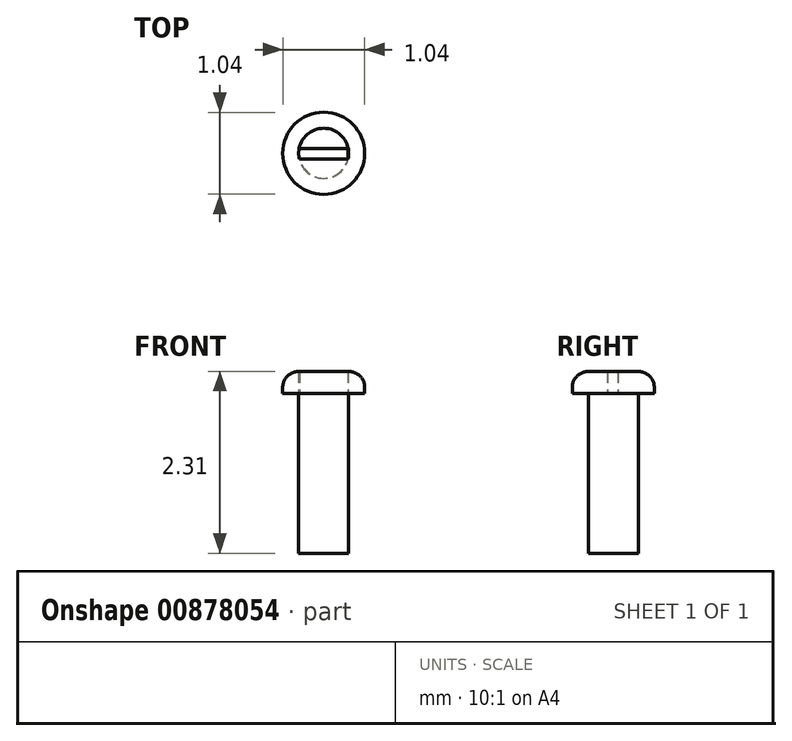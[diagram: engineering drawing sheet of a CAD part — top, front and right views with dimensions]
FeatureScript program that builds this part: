
annotation { "Feature Type Name" : "Feature", "Feature Type Description" : "" }
export const myFeature = defineFeature(function(context is Context, id is Id, definition is map)
    precondition{}
    {
        {
            var Q0;
            Q0=qCreatedBy(makeId("Top.planeOp"),FACE);
            var sketch = newSketch(context, id + "F0", { "sketchPlane" : qUnion([Q0])});
            skCircle(sketch, "E0", {"center": v(0, 0) * mm, "radius": 0.32 * mm});
            skCircle(sketch, "E1", {"center": v(0, 0) * mm, "radius": 0.52 * mm});
            skLineSegment(sketch, "E2.bottom", {"start": v(-0.31, 0.06) * mm, "end": v(0.31, 0.06) * mm});
            skLineSegment(sketch, "E2.top", {"start": v(-0.31, -0.07) * mm, "end": v(0.31, -0.07) * mm});
            skLineSegment(sketch, "E2.left", {"start": v(-0.31, 0.06) * mm, "end": v(-0.31, -0.07) * mm});
            skLineSegment(sketch, "E2.right", {"start": v(0.31, 0.06) * mm, "end": v(0.31, -0.07) * mm});
            skSolve(sketch);
        }
        {
            var Q0;
            {var subQ0=sQuery(id+"F0.wireOp",EDGE,"E2.bottom");Q0=makeQuery(id+"F0.imprint","IMPRINT",FACE,{"disambiguationData":[TD([[makeQuery(id+"F0.imprint","IMPRINT",EDGE,{"derivedFrom":subQ0}),1.0]])]});}
            var Q1;
            {var subQ0=sQuery(id+"F0.wireOp",EDGE,"E2.top");var subQ1=sQuery(id+"F0.wireOp",EDGE,"E0");var subQ3=makeQuery(id+"F0.imprint","INTERSECT",VERTEX,{"derivedFrom":[subQ1,subQ0]});Q1=makeQuery(id+"F0.imprint","IMPRINT",FACE,{"disambiguationData":[TD([[makeQuery(id+"F0.imprint","IMPRINT",EDGE,{"disambiguationData":[TD([[subQ3,-1.0]])],"derivedFrom":subQ1}),1.0]])]});}
            var Q2;
            {var subQ1=sQuery(id+"F0.wireOp",EDGE,"E2.bottom");Q2=makeQuery(id+"F0.imprint","IMPRINT",FACE,{"disambiguationData":[TD([[makeQuery(id+"F0.imprint","IMPRINT",EDGE,{"derivedFrom":subQ1}),-1.0]])]});}
            var Q3;
            {var subQ0=sQuery(id+"F0.wireOp",EDGE,"E2.left");var subQ1=sQuery(id+"F0.wireOp",EDGE,"E0");var subQ3=makeQuery(id+"F0.imprint","INTERSECT",VERTEX,{"derivedFrom":[subQ1,subQ0]});Q3=makeQuery(id+"F0.imprint","IMPRINT",FACE,{"disambiguationData":[TD([[makeQuery(id+"F0.imprint","IMPRINT",EDGE,{"disambiguationData":[TD([[subQ3,1.0]])],"derivedFrom":subQ1}),1.0]])]});}
            extrude(context, id + "F1", {"entities" : qUnion([Q0, Q1, Q2, Q3]), "oppositeDirection" : true, "depth" : 2.03 * mm, "offsetDistance" : 25.4 * mm});
        }
        {
            var Q0;
            Q0 = qSketchRegion(id + "F0", true);
            var Q1;
            {var subQ0=sQuery(id+"F0.wireOp",EDGE,"E2.left");var subQ1=sQuery(id+"F0.wireOp",EDGE,"E0");var subQ2=makeQuery(id+"F0.imprint","INTERSECT",VERTEX,{"derivedFrom":[subQ1,subQ0]});Q1=makeQuery(id+"F0.imprint","IMPRINT",FACE,{"disambiguationData":[TD([[makeQuery(id+"F0.imprint","IMPRINT",EDGE,{"disambiguationData":[TD([[subQ2,-1.0]])],"derivedFrom":subQ1}),-1.0]])]});}
            var Q2;
            {var subQ0=sQuery(id+"F0.wireOp",EDGE,"E2.top");var subQ1=sQuery(id+"F0.wireOp",EDGE,"E0");var subQ3=makeQuery(id+"F0.imprint","INTERSECT",VERTEX,{"derivedFrom":[subQ1,subQ0]});Q2=makeQuery(id+"F0.imprint","IMPRINT",FACE,{"disambiguationData":[TD([[makeQuery(id+"F0.imprint","IMPRINT",EDGE,{"disambiguationData":[TD([[subQ3,-1.0]])],"derivedFrom":subQ1}),1.0]])]});}
            var Q3;
            {var subQ0=sQuery(id+"F0.wireOp",EDGE,"E2.bottom");Q3=makeQuery(id+"F0.imprint","IMPRINT",FACE,{"disambiguationData":[TD([[makeQuery(id+"F0.imprint","IMPRINT",EDGE,{"derivedFrom":subQ0}),1.0]])]});}
            extrude(context, id + "F2", {"entities" : qUnion([Q0, Q1, Q2, Q3]), "depth" : 0.28 * mm, "offsetDistance" : 25.4 * mm});
        }
        {
            var Q0;
            Q0=makeQuery(id+"F2.opExtrude","CAP_EDGE",EDGE,{"disambiguationData":[OSD([sQuery(id+"F0.wireOp",EDGE,"E1")])],"isStart":false});
            fillet(context, id + "F3", {"entities" : qUnion([Q0]), "radius" : 0.2 * mm, "tangentPropagation" : true, "allowEdgeOverflow" : false});
        }
    });
